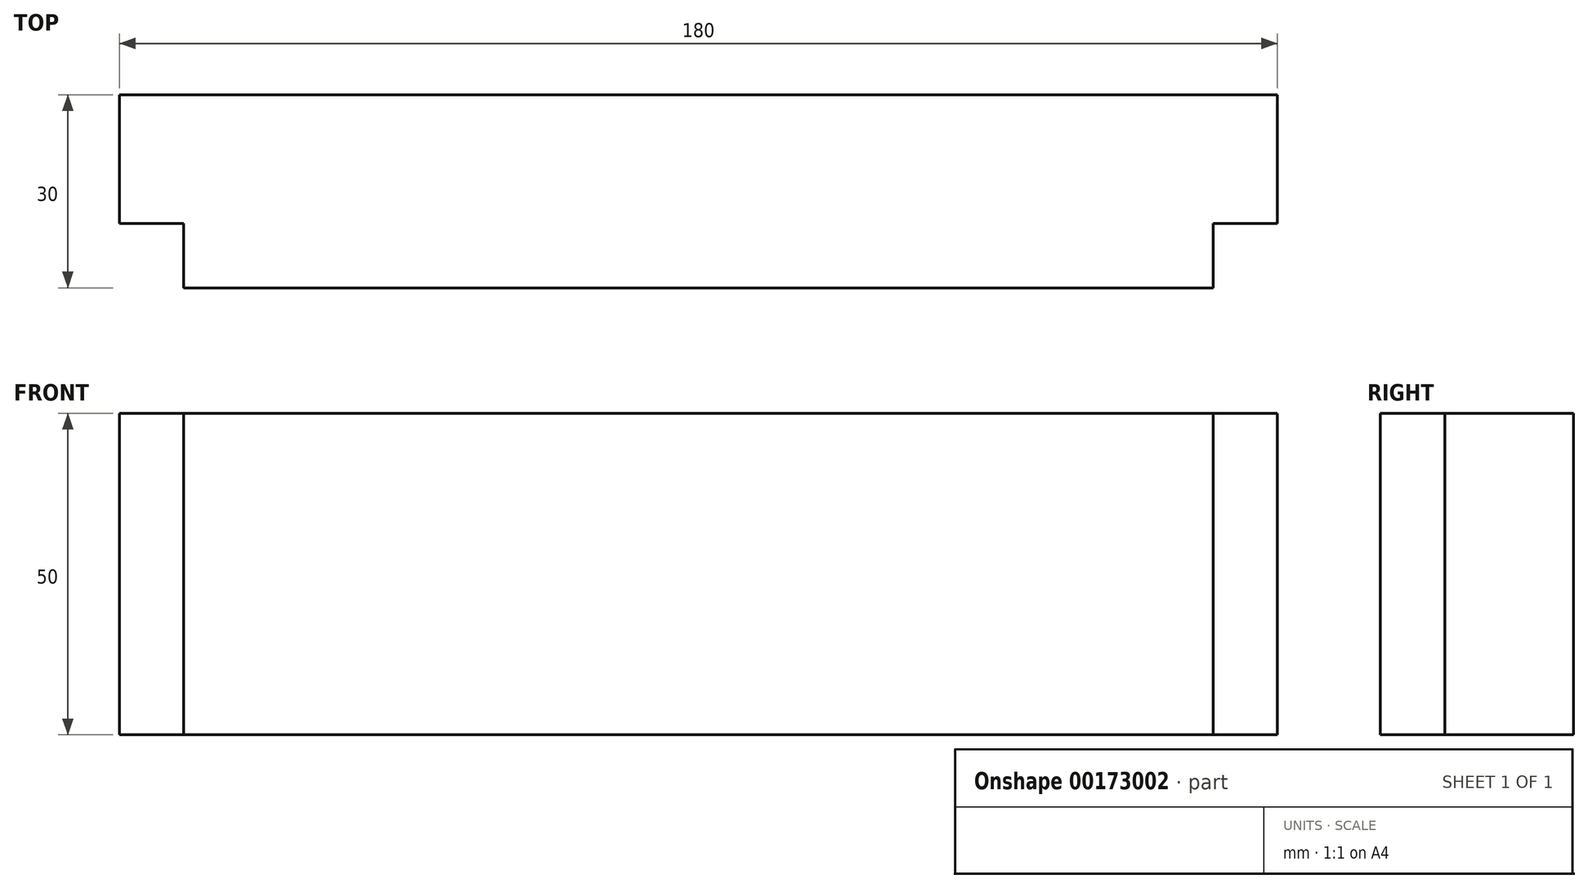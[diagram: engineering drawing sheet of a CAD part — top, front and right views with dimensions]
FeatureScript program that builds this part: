
annotation { "Feature Type Name" : "Feature", "Feature Type Description" : "" }
export const myFeature = defineFeature(function(context is Context, id is Id, definition is map)
    precondition{}
    {
        {
            var Q0;
            Q0=qCreatedBy(makeId("Top.planeOp"),FACE);
            var sketch = newSketch(context, id + "F0", { "sketchPlane" : qUnion([Q0])});
            skLineSegment(sketch, "E0", {"start": v(80, 0) * mm, "end": v(80, 10) * mm});
            skLineSegment(sketch, "E1", {"start": v(80, 10) * mm, "end": v(90, 10) * mm});
            skLineSegment(sketch, "E2", {"start": v(90, 10) * mm, "end": v(90, 30) * mm});
            skLineSegment(sketch, "E3", {"start": v(90, 30) * mm, "end": v(0, 30) * mm});
            skLineSegment(sketch, "E4", {"start": v(80, 0) * mm, "end": v(0, 0) * mm});
            skLineSegment(sketch, "E5", {"start": v(0, 0) * mm, "end": v(0, 30) * mm, "construction": true});
            skLineSegment(sketch, "E6.MirrorCS", {"start": v(-90, 30) * mm, "end": v(0, 30) * mm});
            skLineSegment(sketch, "E7.MirrorCS", {"start": v(-90, 10) * mm, "end": v(-90, 30) * mm});
            skLineSegment(sketch, "E8.MirrorCS", {"start": v(-80, 10) * mm, "end": v(-90, 10) * mm});
            skLineSegment(sketch, "E9.MirrorCS", {"start": v(-80, 0) * mm, "end": v(-80, 10) * mm});
            skLineSegment(sketch, "E10.MirrorCS", {"start": v(-80, 0) * mm, "end": v(0, 0) * mm});
            skSolve(sketch);
        }
        {
            var Q0;
            Q0 = qSketchRegion(id + "F0", true);
            extrude(context, id + "F1", {"entities" : qUnion([Q0]), "depth" : 50 * mm});
        }
    });
